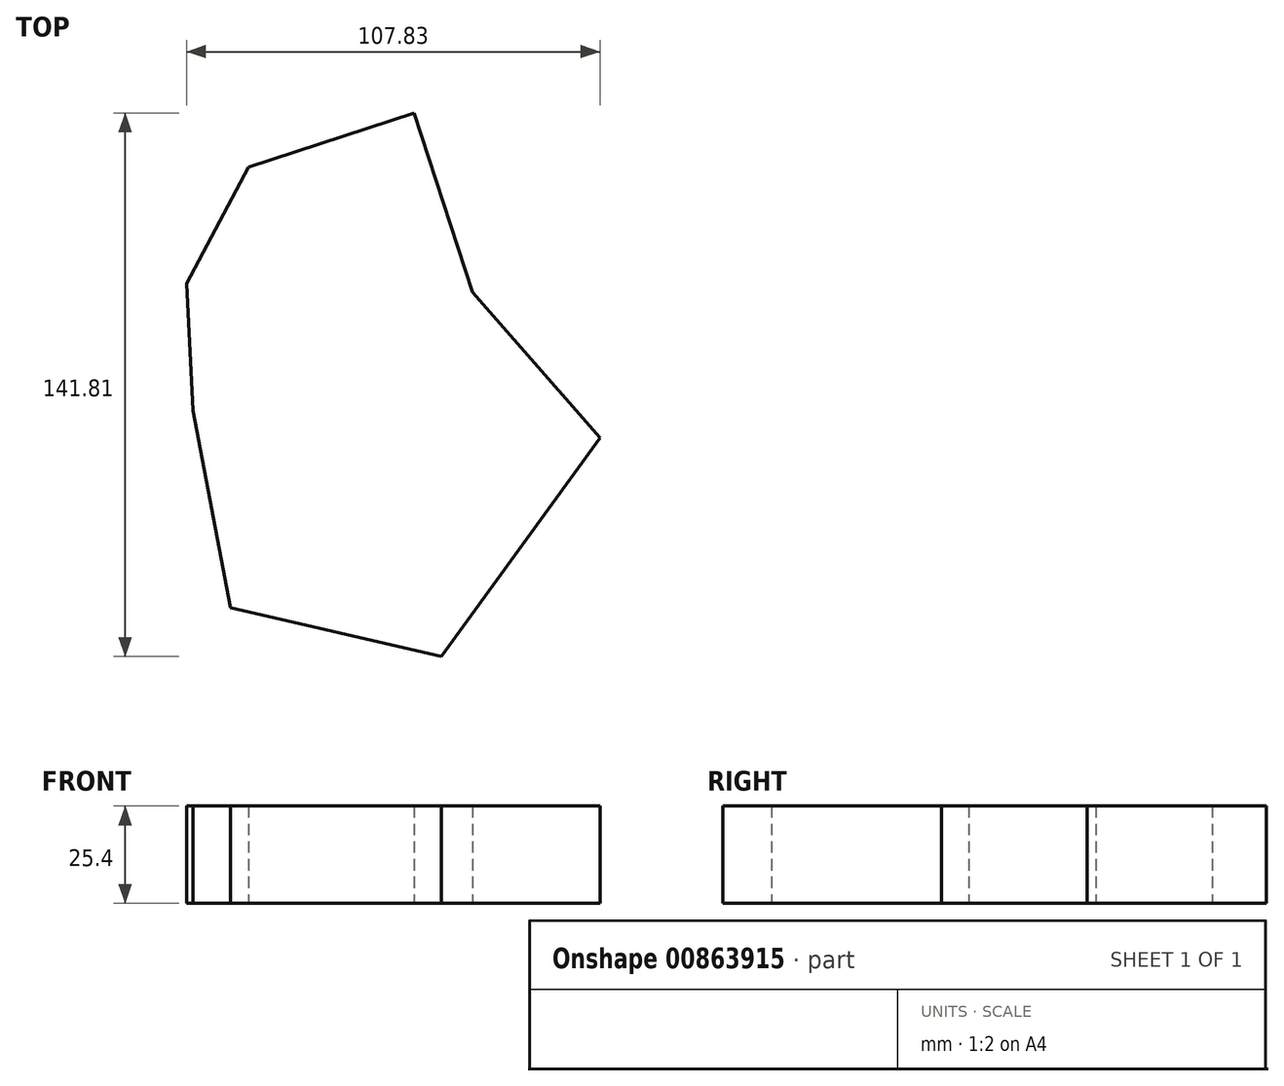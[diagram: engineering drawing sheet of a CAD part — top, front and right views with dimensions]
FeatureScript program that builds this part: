
annotation { "Feature Type Name" : "Feature", "Feature Type Description" : "" }
export const myFeature = defineFeature(function(context is Context, id is Id, definition is map)
    precondition{}
    {
        {
            var Q0;
            Q0=qCreatedBy(makeId("Top.planeOp"),FACE);
            var sketch = newSketch(context, id + "F0", { "sketchPlane" : qUnion([Q0])});
            skLineSegment(sketch, "E0", {"start": v(-32.2, 26.7) * mm, "end": v(-22.53, -24.69) * mm});
            skLineSegment(sketch, "E1", {"start": v(-22.53, -24.69) * mm, "end": v(32.5, -37.46) * mm});
            skLineSegment(sketch, "E2", {"start": v(32.5, -37.46) * mm, "end": v(73.88, 19.56) * mm});
            skLineSegment(sketch, "E3", {"start": v(73.88, 19.56) * mm, "end": v(40.67, 57.52) * mm});
            skLineSegment(sketch, "E4", {"start": v(40.67, 57.52) * mm, "end": v(25.36, 104.35) * mm});
            skLineSegment(sketch, "E5", {"start": v(25.36, 104.35) * mm, "end": v(-17.8, 90.24) * mm});
            skLineSegment(sketch, "E6", {"start": v(-17.8, 90.24) * mm, "end": v(-33.95, 59.85) * mm});
            skLineSegment(sketch, "E7", {"start": v(-33.95, 59.85) * mm, "end": v(-32.2, 26.7) * mm});
            skSolve(sketch);
        }
        {
            var Q0;
            Q0=makeQuery(id+"F0.imprint","IMPRINT",FACE,{"disambiguationData":[TD([[makeQuery(id+"F0.imprint","IMPRINT",EDGE,{"derivedFrom":sQuery(id+"F0.wireOp",EDGE,"E0")}),1.0]])]});
            extrude(context, id + "F1", {"entities" : qUnion([Q0]), "depth" : 25.4 * mm, "offsetDistance" : 25.4 * mm});
        }
    });
